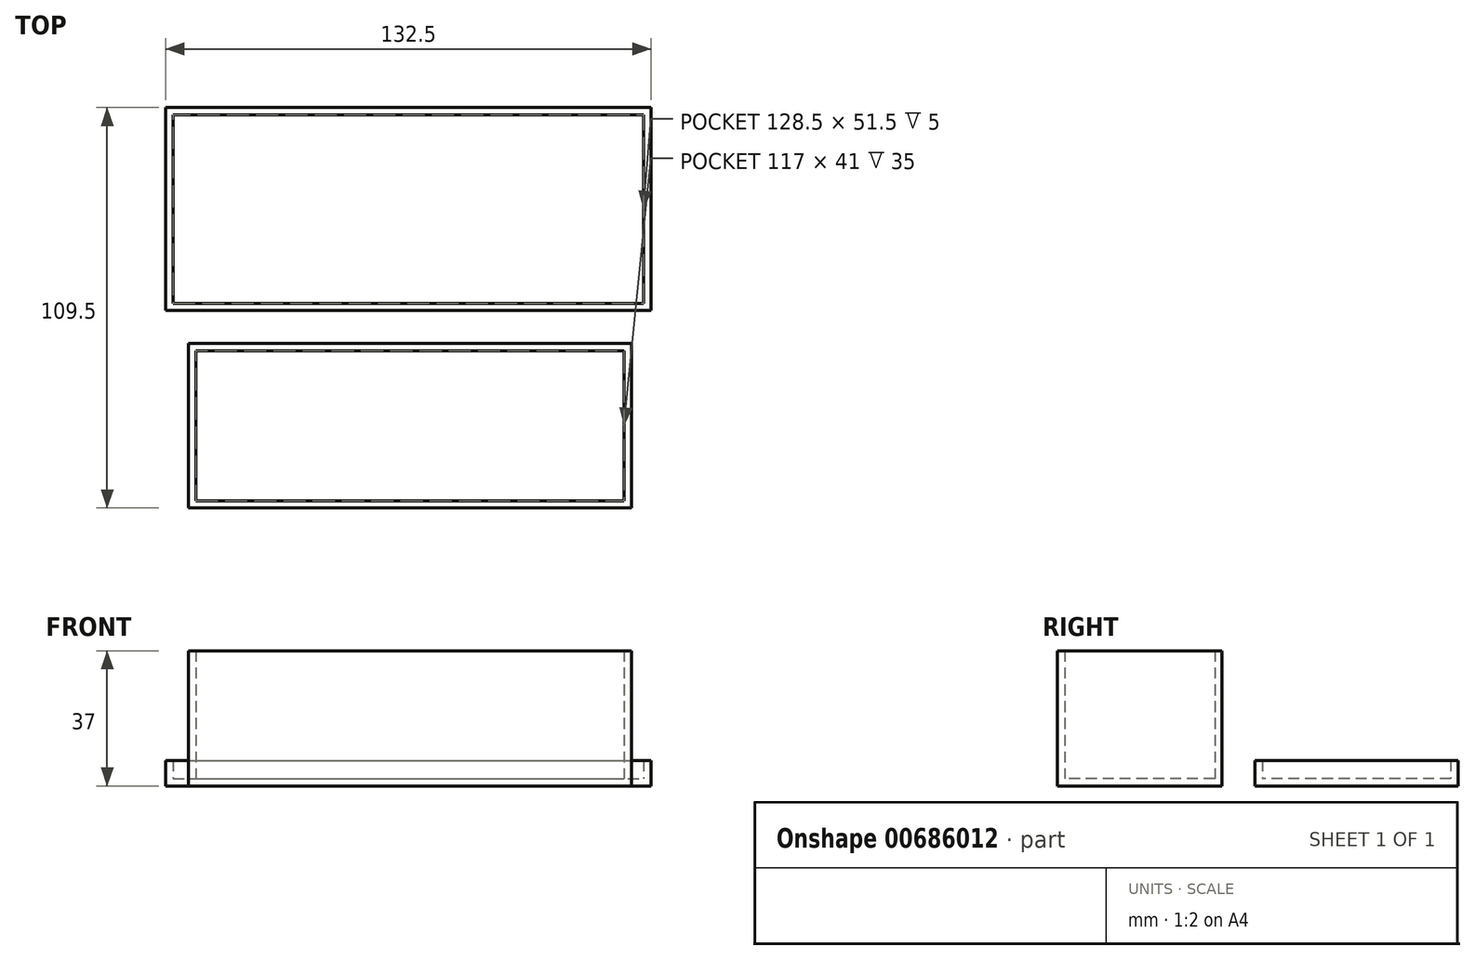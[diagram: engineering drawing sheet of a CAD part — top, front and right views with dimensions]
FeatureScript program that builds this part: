
annotation { "Feature Type Name" : "Feature", "Feature Type Description" : "" }
export const myFeature = defineFeature(function(context is Context, id is Id, definition is map)
    precondition{}
    {
        {
            var Q0;
            Q0=qCreatedBy(makeId("Top.planeOp"),FACE);
            var sketch = newSketch(context, id + "F0", { "sketchPlane" : qUnion([Q0])});
            skLineSegment(sketch, "E0.bottom", {"start": v(-62.77, 59.84) * mm, "end": v(69.73, 59.84) * mm});
            skLineSegment(sketch, "E0.top", {"start": v(-62.77, 4.34) * mm, "end": v(69.73, 4.34) * mm});
            skLineSegment(sketch, "E0.left", {"start": v(-62.77, 59.84) * mm, "end": v(-62.77, 4.34) * mm});
            skLineSegment(sketch, "E0.right", {"start": v(69.73, 59.84) * mm, "end": v(69.73, 4.34) * mm});
            skLineSegment(sketch, "E1.bottom", {"start": v(-56.6, -4.66) * mm, "end": v(64.4, -4.66) * mm});
            skLineSegment(sketch, "E1.top", {"start": v(-56.6, -49.66) * mm, "end": v(64.4, -49.66) * mm});
            skLineSegment(sketch, "E1.left", {"start": v(-56.6, -4.66) * mm, "end": v(-56.6, -49.66) * mm});
            skLineSegment(sketch, "E1.right", {"start": v(64.4, -4.66) * mm, "end": v(64.4, -49.66) * mm});
            skLineSegment(sketch, "E2.0", {"start": v(-60.77, 57.84) * mm, "end": v(67.73, 57.84) * mm});
            skLineSegment(sketch, "E2.1", {"start": v(-60.77, 57.84) * mm, "end": v(-60.77, 6.34) * mm});
            skLineSegment(sketch, "E2.2", {"start": v(-60.77, 6.34) * mm, "end": v(67.73, 6.34) * mm});
            skLineSegment(sketch, "E2.3", {"start": v(67.73, 57.84) * mm, "end": v(67.73, 6.34) * mm});
            skLineSegment(sketch, "E3.0", {"start": v(-54.6, -6.66) * mm, "end": v(62.4, -6.66) * mm});
            skLineSegment(sketch, "E3.1", {"start": v(-54.6, -6.66) * mm, "end": v(-54.6, -47.66) * mm});
            skLineSegment(sketch, "E3.2", {"start": v(-54.6, -47.66) * mm, "end": v(62.4, -47.66) * mm});
            skLineSegment(sketch, "E3.3", {"start": v(62.4, -6.66) * mm, "end": v(62.4, -47.66) * mm});
            skSolve(sketch);
        }
        {
            var Q0;
            Q0=makeQuery(id+"F0.imprint","IMPRINT",FACE,{"disambiguationData":[TD([[makeQuery(id+"F0.imprint","IMPRINT",EDGE,{"derivedFrom":sQuery(id+"F0.wireOp",EDGE,"E0.bottom")}),-1.0]])]});
            var Q1;
            Q1=makeQuery(id+"F0.imprint","IMPRINT",FACE,{"disambiguationData":[TD([[makeQuery(id+"F0.imprint","IMPRINT",EDGE,{"derivedFrom":sQuery(id+"F0.wireOp",EDGE,"E2.0")}),-1.0]])]});
            var Q2;
            Q2=makeQuery(id+"F0.imprint","IMPRINT",FACE,{"disambiguationData":[TD([[makeQuery(id+"F0.imprint","IMPRINT",EDGE,{"derivedFrom":sQuery(id+"F0.wireOp",EDGE,"E1.bottom")}),-1.0]])]});
            var Q3;
            Q3=makeQuery(id+"F0.imprint","IMPRINT",FACE,{"disambiguationData":[TD([[makeQuery(id+"F0.imprint","IMPRINT",EDGE,{"derivedFrom":sQuery(id+"F0.wireOp",EDGE,"E3.0")}),-1.0]])]});
            extrude(context, id + "F1", {"entities" : qUnion([Q0, Q1, Q2, Q3]), "oppositeDirection" : true, "depth" : 2 * mm, "offsetDistance" : 25 * mm});
        }
        {
            var Q0;
            Q0=makeQuery(id+"F0.imprint","IMPRINT",FACE,{"disambiguationData":[TD([[makeQuery(id+"F0.imprint","IMPRINT",EDGE,{"derivedFrom":sQuery(id+"F0.wireOp",EDGE,"E0.bottom")}),-1.0]])]});
            extrude(context, id + "F2", {"entities" : qUnion([Q0]), "operationType" : NewBodyOperationType.ADD, "depth" : 5 * mm, "offsetDistance" : 25 * mm});
        }
        {
            var Q0;
            Q0=makeQuery(id+"F0.imprint","IMPRINT",FACE,{"disambiguationData":[TD([[makeQuery(id+"F0.imprint","IMPRINT",EDGE,{"derivedFrom":sQuery(id+"F0.wireOp",EDGE,"E1.bottom")}),-1.0]])]});
            extrude(context, id + "F3", {"entities" : qUnion([Q0]), "operationType" : NewBodyOperationType.ADD, "depth" : 35 * mm, "offsetDistance" : 25 * mm});
        }
    });
